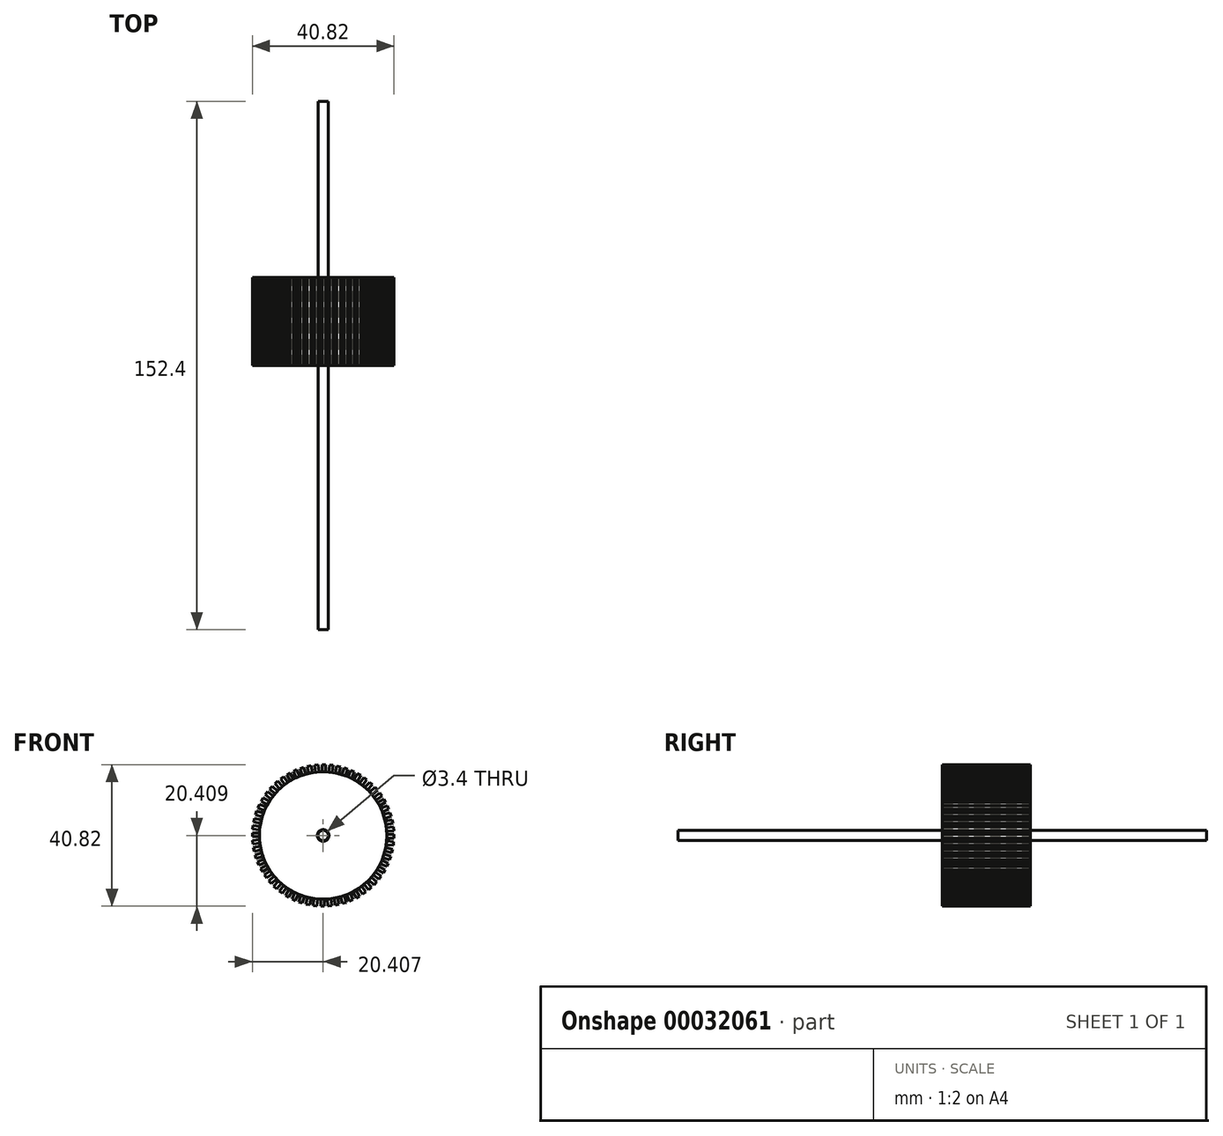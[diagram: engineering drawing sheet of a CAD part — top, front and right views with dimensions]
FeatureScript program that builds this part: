
annotation { "Feature Type Name" : "Feature", "Feature Type Description" : "" }
export const myFeature = defineFeature(function(context is Context, id is Id, definition is map)
    precondition{}
    {
        {
            var Q0;
            Q0=qCreatedBy(makeId("Front.planeOp"),FACE);
            var sketch = newSketch(context, id + "F0", { "sketchPlane" : qUnion([Q0])});
            skCircle(sketch, "E0", {"center": v(-36.56, 11.85) * mm, "radius": 18.37 * mm});
            skCircle(sketch, "E1", {"center": v(-36.56, 11.85) * mm, "radius": 1.7 * mm});
            skSolve(sketch);
        }
        {
            var Q0;
            Q0=qCreatedBy(makeId("Front.planeOp"),FACE);
            var sketch = newSketch(context, id + "F1", { "sketchPlane" : qUnion([Q0])});
            skLineSegment(sketch, "E2.bottom", {"start": v(-36.9, 30.23) * mm, "end": v(-35.82, 30.23) * mm});
            skLineSegment(sketch, "E2.top", {"start": v(-36.9, 32.26) * mm, "end": v(-35.82, 32.26) * mm});
            skLineSegment(sketch, "E2.left", {"start": v(-36.9, 30.23) * mm, "end": v(-36.9, 32.26) * mm});
            skLineSegment(sketch, "E2.right", {"start": v(-35.82, 30.23) * mm, "end": v(-35.82, 32.26) * mm});
            skSolve(sketch);
        }
        {
            var Q0;
            Q0 = qSketchRegion(id + "F1", true);
            extrude(context, id + "F2", {"entities" : qUnion([Q0]), "depth" : 25.4 * mm});
        }
        {
            var Q0;
            Q0=makeQuery(id+"F0.imprint","IMPRINT",FACE,{"disambiguationData":[TD([[makeQuery(id+"F0.imprint","IMPRINT",EDGE,{"derivedFrom":sQuery(id+"F0.wireOp",EDGE,"E0")}),1.0]])]});
            var Q1;
            Q1=sQuery(id+"F0.wireOp",EDGE,"E0");
            extrude(context, id + "F3", {"entities" : qUnion([Q0]), "surfaceEntities" : qUnion([Q1]), "depth" : 25.4 * mm});
        }
        {
            var Q0;
            Q0=makeQuery(id+"F2.opExtrude","SWEPT_BODY",BODY,{"disambiguationData":[OSD([sQuery(id+"F1.wireOp",EDGE,"E2.bottom"),sQuery(id+"F1.wireOp",EDGE,"E2.top"),sQuery(id+"F1.wireOp",EDGE,"E2.left"),sQuery(id+"F1.wireOp",EDGE,"E2.right")])]});
            var Q1;
            Q1=makeQuery(id+"F3.opExtrude","CAP_EDGE",EDGE,{"disambiguationData":[OSD([sQuery(id+"F0.wireOp",EDGE,"E0")])],"isStart":false});
            circularPattern(context, id + "F4", {"operationType" : NewBodyOperationType.ADD, "entities" : qUnion([Q0]), "axis" : qUnion([Q1]), "angle" : 360 * degree, "instanceCount" : 60, "oppositeDirection" : true, "equalSpace" : true});
        }
        {
            var Q0;
            Q0=makeQuery(id+"F3.opExtrude","CAP_FACE",FACE,{"disambiguationData":[OSD([sQuery(id+"F0.wireOp",EDGE,"E0"),sQuery(id+"F0.wireOp",EDGE,"E1")])],"isStart":false});
            var sketch = newSketch(context, id + "F5", { "sketchPlane" : qUnion([Q0])});
            skCircle(sketch, "E3", {"center": v(-36.56, 11.85) * mm, "radius": 1.47 * mm});
            skSolve(sketch);
        }
        {
            var Q0;
            Q0=makeQuery(id+"F5.imprint","IMPRINT",FACE,{"disambiguationData":[TD([[makeQuery(id+"F5.imprint","IMPRINT",EDGE,{"derivedFrom":sQuery(id+"F5.wireOp",EDGE,"E3")}),1.0]])]});
            extrude(context, id + "F6", {"entities" : qUnion([Q0]), "operationType" : NewBodyOperationType.ADD, "endBound" : BoundingType.SYMMETRIC, "oppositeDirection" : true, "depth" : 152.4 * mm});
        }
    });
